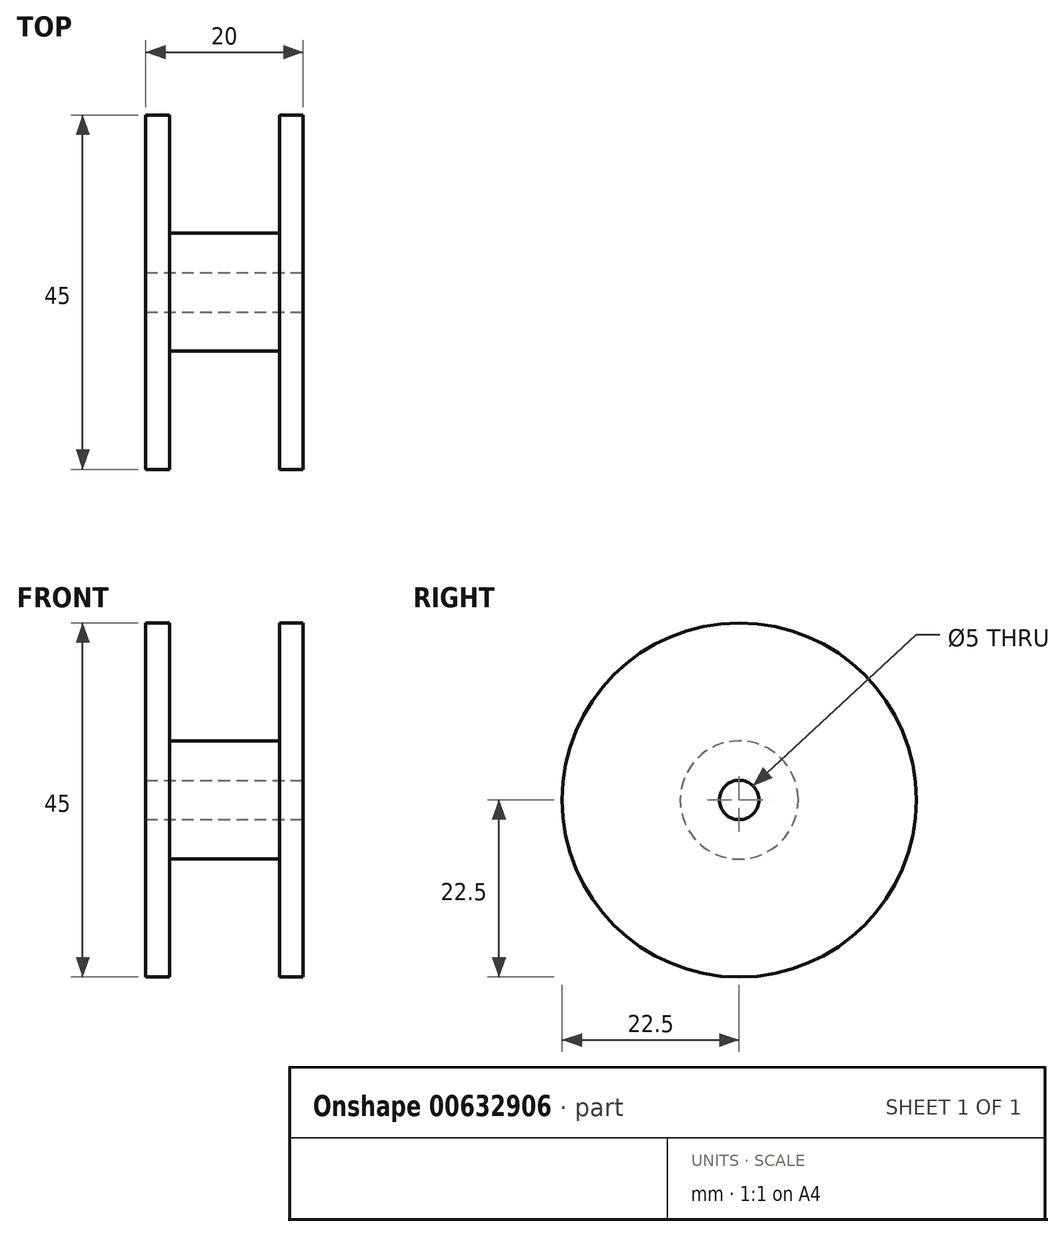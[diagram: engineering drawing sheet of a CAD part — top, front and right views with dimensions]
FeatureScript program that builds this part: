
annotation { "Feature Type Name" : "Feature", "Feature Type Description" : "" }
export const myFeature = defineFeature(function(context is Context, id is Id, definition is map)
    precondition{}
    {
        {
            var Q0;
            Q0=qCreatedBy(makeId("Front.planeOp"),FACE);
            var sketch = newSketch(context, id + "F0", { "sketchPlane" : qUnion([Q0])});
            skLineSegment(sketch, "E0", {"start": v(0, 7.5) * mm, "end": v(-7, 7.5) * mm});
            skLineSegment(sketch, "E1", {"start": v(-7, 7.5) * mm, "end": v(-7, 22.5) * mm});
            skLineSegment(sketch, "E2", {"start": v(-7, 22.5) * mm, "end": v(-10, 22.5) * mm});
            skLineSegment(sketch, "E3", {"start": v(-10, 22.5) * mm, "end": v(-10, 2.5) * mm});
            skLineSegment(sketch, "E4.MirrorCS", {"start": v(7, 22.5) * mm, "end": v(10, 22.5) * mm});
            skLineSegment(sketch, "E5.MirrorCS", {"start": v(7, 7.5) * mm, "end": v(7, 22.5) * mm});
            skLineSegment(sketch, "E6.MirrorCS", {"start": v(0, 7.5) * mm, "end": v(7, 7.5) * mm});
            skLineSegment(sketch, "E7.MirrorCS", {"start": v(10, 22.5) * mm, "end": v(10, 2.5) * mm});
            skLineSegment(sketch, "E8", {"start": v(-10, 2.5) * mm, "end": v(10, 2.5) * mm});
            skLineSegment(sketch, "E9", {"start": v(0, 0) * mm, "end": v(-4.65, 0) * mm});
            skSolve(sketch);
        }
        {
            var Q0;
            Q0=makeQuery(id+"F0.imprint","IMPRINT",FACE,{"disambiguationData":[TD([[makeQuery(id+"F0.imprint","IMPRINT",EDGE,{"derivedFrom":sQuery(id+"F0.wireOp",EDGE,"E0")}),1.0]])]});
            var Q1;
            Q1=sQuery(id+"F0.wireOp",EDGE,"E9");
            revolve(context, id + "F1", {"entities" : qUnion([Q0]), "axis" : qUnion([Q1]), "revolveType" : RevolveType.FULL});
        }
    });
